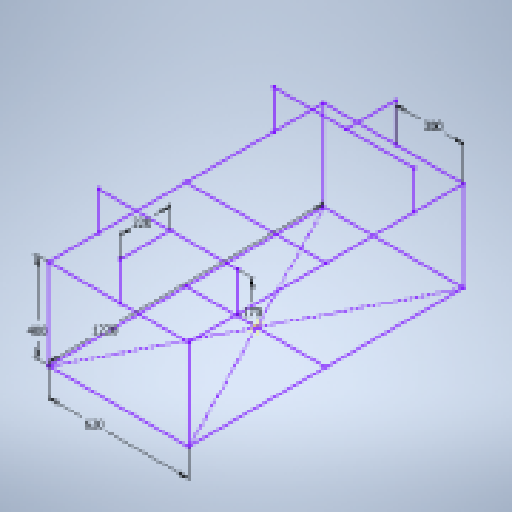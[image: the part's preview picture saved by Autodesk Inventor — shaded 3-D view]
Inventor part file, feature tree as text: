
AUTODESK INVENTOR PART (.ipt)
format: ipt  version: 2025.1 (Build 291241020, 241B)  size: 146,432 bytes
history: native  units: in
note: dims shown in document units (in); Inventor stores cm internally (conversion verified against a paired STEP export)
features: sketch x2
ambient origin geometry x8: Origin, YZ Plane, XZ Plane, XY Plane, X Axis, Y Axis, Z Axis, Center Point
feature tree (2):
  sketch  "Sketch3"  dims[d4=48.0315in d5=24.4094in d6=15.748in d7=6.6929in d8=8.6614in d9=11.811in]
  sketch  "3D Sketch3"
